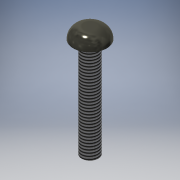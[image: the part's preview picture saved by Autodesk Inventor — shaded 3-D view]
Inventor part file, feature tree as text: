
AUTODESK INVENTOR PART (.ipt)
format: ipt  version: 2020.2 (Build 242310000, 310)  size: 139,776 bytes
history: native  units: mm
features: extrude x4, sketch x4, other x1, fillet x1, thread x1
ambient origin geometry x1: Origin
bodies: Body1 (feature_tree)
feature tree (11):
  other  "ソリッド1"
  extrude  "押し出し1"  Depth=3.0mm
  extrude  "押し出し2"  Depth=6.0mm TaperAngle=0.0deg
  fillet  "フィレット1"  Radius=6.0mm
  thread  "ねじ1"
  extrude  "押し出し3"  Depth=2.0mm TaperAngle=0.0deg
  extrude  "押し出し4"  Depth=2.0mm
  sketch  "スケッチ1"
  sketch  "スケッチ2"
  sketch  "スケッチ3"
  sketch  "スケッチ4"
